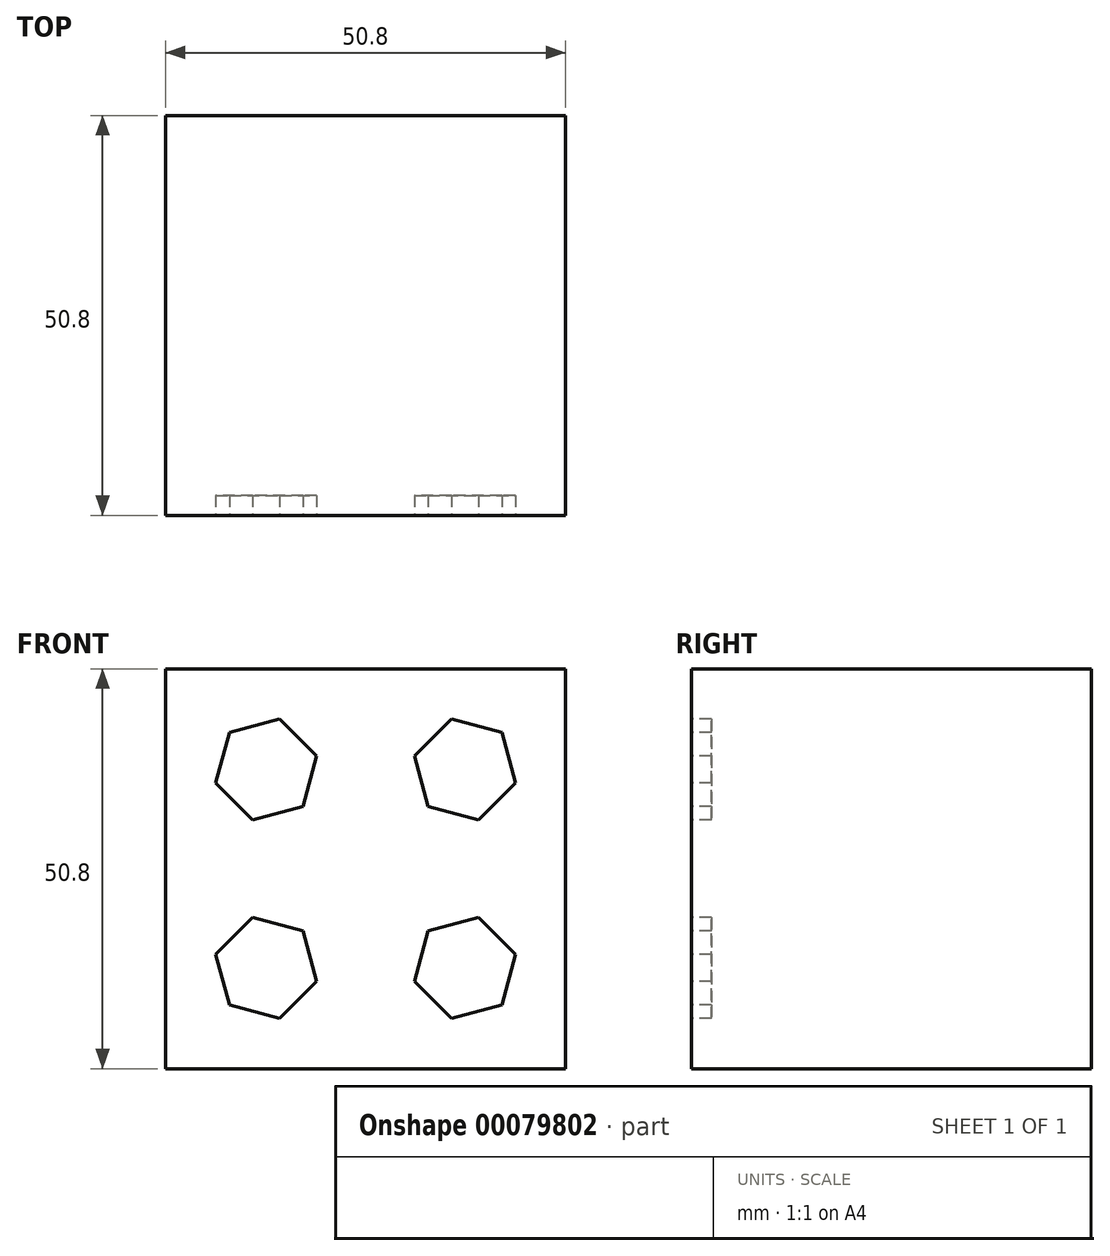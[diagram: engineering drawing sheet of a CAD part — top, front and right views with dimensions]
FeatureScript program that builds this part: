
annotation { "Feature Type Name" : "Feature", "Feature Type Description" : "" }
export const myFeature = defineFeature(function(context is Context, id is Id, definition is map)
    precondition{}
    {
        {
            var Q0;
            Q0=qCreatedBy(makeId("Front.planeOp"),FACE);
            var sketch = newSketch(context, id + "F0", { "sketchPlane" : qUnion([Q0])});
            skLineSegment(sketch, "E0.bottom", {"start": v(0, 0) * mm, "end": v(50.8, 0) * mm});
            skLineSegment(sketch, "E0.top", {"start": v(0, 50.8) * mm, "end": v(50.8, 50.8) * mm});
            skLineSegment(sketch, "E0.left", {"start": v(0, 0) * mm, "end": v(0, 50.8) * mm});
            skLineSegment(sketch, "E0.right", {"start": v(50.8, 0) * mm, "end": v(50.8, 50.8) * mm});
            skSolve(sketch);
        }
        {
            var Q0;
            Q0=makeQuery(id+"F0.imprint","IMPRINT",FACE,{"disambiguationData":[TD([[makeQuery(id+"F0.imprint","IMPRINT",EDGE,{"derivedFrom":sQuery(id+"F0.wireOp",EDGE,"E0.bottom")}),1.0]])]});
            extrude(context, id + "F1", {"entities" : qUnion([Q0]), "depth" : 50.8 * mm});
        }
        {
            var Q0;
            Q0=makeQuery(id+"F1.opExtrude","CAP_FACE",FACE,{"disambiguationData":[OSD([sQuery(id+"F0.wireOp",EDGE,"E0.bottom"),sQuery(id+"F0.wireOp",EDGE,"E0.top"),sQuery(id+"F0.wireOp",EDGE,"E0.left"),sQuery(id+"F0.wireOp",EDGE,"E0.right")])],"isStart":false});
            var sketch = newSketch(context, id + "F2", { "sketchPlane" : qUnion([Q0])});
            skLineSegment(sketch, "E1", {"start": v(0, 50.8) * mm, "end": v(50.8, 0) * mm, "construction": true});
            skLineSegment(sketch, "E2", {"start": v(50.8, 50.8) * mm, "end": v(0, 0) * mm, "construction": true});
            skLineSegment(sketch, "E3", {"start": v(25.4, 50.8) * mm, "end": v(25.4, 0) * mm, "construction": true});
            skLineSegment(sketch, "E4", {"start": v(0, 25.4) * mm, "end": v(50.8, 25.4) * mm, "construction": true});
            skCircle(sketch, "E5.cCircle", {"center": v(12.79, 38.01) * mm, "radius": 5.74 * mm, "construction": true});
            skLineSegment(sketch, "E5.0", {"start": v(14.5, 44.42) * mm, "end": v(19.2, 39.73) * mm});
            skLineSegment(sketch, "E5.1", {"start": v(19.2, 39.73) * mm, "end": v(17.48, 33.32) * mm});
            skLineSegment(sketch, "E5.2", {"start": v(17.48, 33.32) * mm, "end": v(11.07, 31.6) * mm});
            skLineSegment(sketch, "E5.3", {"start": v(11.07, 31.6) * mm, "end": v(6.38, 36.3) * mm});
            skLineSegment(sketch, "E5.4", {"start": v(6.38, 36.3) * mm, "end": v(8.1, 42.7) * mm});
            skLineSegment(sketch, "E5.5", {"start": v(8.1, 42.7) * mm, "end": v(14.5, 44.42) * mm});
            skPoint(sketch, "E5.0.midPoint", {"position": v(16.85, 42.07) * mm});
            skLineSegment(sketch, "E6.MirrorCS", {"start": v(42.7, 42.7) * mm, "end": v(36.3, 44.42) * mm});
            skLineSegment(sketch, "E7.MirrorCS", {"start": v(44.42, 36.3) * mm, "end": v(42.7, 42.7) * mm});
            skLineSegment(sketch, "E8.MirrorCS", {"start": v(39.73, 31.6) * mm, "end": v(44.42, 36.3) * mm});
            skLineSegment(sketch, "E9.MirrorCS", {"start": v(33.32, 33.32) * mm, "end": v(39.73, 31.6) * mm});
            skLineSegment(sketch, "E10.MirrorCS", {"start": v(31.6, 39.73) * mm, "end": v(33.32, 33.32) * mm});
            skLineSegment(sketch, "E11.MirrorCS", {"start": v(36.3, 44.42) * mm, "end": v(31.6, 39.73) * mm});
            skLineSegment(sketch, "E12.MirrorCS", {"start": v(19.2, 11.07) * mm, "end": v(17.48, 17.48) * mm});
            skLineSegment(sketch, "E13.MirrorCS", {"start": v(14.5, 6.38) * mm, "end": v(19.2, 11.07) * mm});
            skLineSegment(sketch, "E14.MirrorCS", {"start": v(17.48, 17.48) * mm, "end": v(11.07, 19.2) * mm});
            skCircle(sketch, "E15.MirrorC", {"center": v(12.79, 12.79) * mm, "radius": 5.74 * mm, "construction": true});
            skLineSegment(sketch, "E16.MirrorCS", {"start": v(11.07, 19.2) * mm, "end": v(6.38, 14.5) * mm});
            skLineSegment(sketch, "E17.MirrorCS", {"start": v(6.38, 14.5) * mm, "end": v(8.1, 8.1) * mm});
            skLineSegment(sketch, "E18.MirrorCS", {"start": v(31.6, 11.07) * mm, "end": v(33.32, 17.48) * mm});
            skLineSegment(sketch, "E19.MirrorCS", {"start": v(33.32, 17.48) * mm, "end": v(39.73, 19.2) * mm});
            skLineSegment(sketch, "E20.MirrorCS", {"start": v(39.73, 19.2) * mm, "end": v(44.42, 14.5) * mm});
            skPoint(sketch, "E21.MirrorP", {"position": v(16.85, 8.73) * mm});
            skLineSegment(sketch, "E22.MirrorCS", {"start": v(42.7, 8.1) * mm, "end": v(36.3, 6.38) * mm});
            skLineSegment(sketch, "E23.MirrorCS", {"start": v(44.42, 14.5) * mm, "end": v(42.7, 8.1) * mm});
            skLineSegment(sketch, "E24.MirrorCS", {"start": v(8.1, 8.1) * mm, "end": v(14.5, 6.38) * mm});
            skLineSegment(sketch, "E25.MirrorCS", {"start": v(36.3, 6.38) * mm, "end": v(31.6, 11.07) * mm});
            skSolve(sketch);
        }
        {
            var Q0;
            Q0=makeQuery(id+"F2.imprint","IMPRINT",FACE,{"disambiguationData":[TD([[makeQuery(id+"F2.imprint","IMPRINT",EDGE,{"derivedFrom":sQuery(id+"F2.wireOp",EDGE,"E5.0")}),-1.0]])]});
            var Q1;
            Q1=makeQuery(id+"F2.imprint","IMPRINT",FACE,{"disambiguationData":[TD([[makeQuery(id+"F2.imprint","IMPRINT",EDGE,{"derivedFrom":sQuery(id+"F2.wireOp",EDGE,"E6.MirrorCS")}),1.0]])]});
            var Q2;
            Q2=makeQuery(id+"F2.imprint","IMPRINT",FACE,{"disambiguationData":[TD([[makeQuery(id+"F2.imprint","IMPRINT",EDGE,{"derivedFrom":sQuery(id+"F2.wireOp",EDGE,"E12.MirrorCS")}),1.0]])]});
            var Q3;
            Q3=makeQuery(id+"F2.imprint","IMPRINT",FACE,{"disambiguationData":[TD([[makeQuery(id+"F2.imprint","IMPRINT",EDGE,{"derivedFrom":sQuery(id+"F2.wireOp",EDGE,"E18.MirrorCS")}),-1.0]])]});
            extrude(context, id + "F3", {"entities" : qUnion([Q0, Q1, Q2, Q3]), "operationType" : NewBodyOperationType.REMOVE, "oppositeDirection" : true, "depth" : 2.54 * mm});
        }
    });
